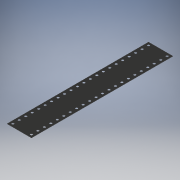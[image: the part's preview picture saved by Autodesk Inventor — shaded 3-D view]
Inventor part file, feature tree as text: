
AUTODESK INVENTOR PART (.ipt)
format: ipt  version: 2019 (Build 230136000, 136)  size: 162,816 bytes
history: native  units: mm
features: extrude x1, other x1
ambient origin geometry x8: Origin, YZ Plane, XZ Plane, XY Plane, X Axis, Y Axis, Z Axis, Center Point
bodies: Body1 (feature_tree)
feature tree (2):
  extrude  "Foam Body"  Depth=1094.0mm
  other  "Foam Scheme"
